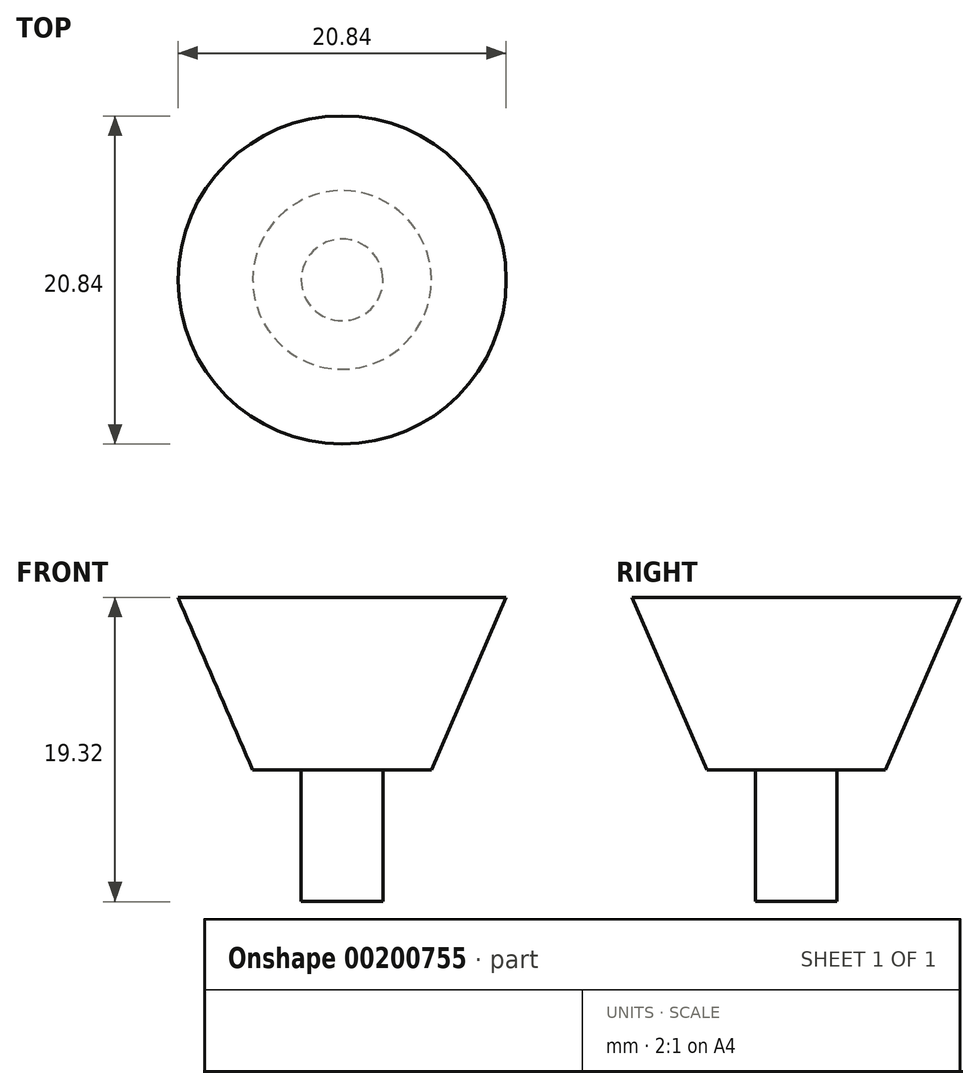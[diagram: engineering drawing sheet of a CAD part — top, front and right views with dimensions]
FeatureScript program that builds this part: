
annotation { "Feature Type Name" : "Feature", "Feature Type Description" : "" }
export const myFeature = defineFeature(function(context is Context, id is Id, definition is map)
    precondition{}
    {
        {
            var Q0;
            Q0=qCreatedBy(makeId("Front.planeOp"),FACE);
            var sketch = newSketch(context, id + "F0", { "sketchPlane" : qUnion([Q0])});
            skLineSegment(sketch, "E0", {"start": v(0, 0) * mm, "end": v(10.42, 0) * mm});
            skLineSegment(sketch, "E1", {"start": v(10.42, 0) * mm, "end": v(5.67, -10.95) * mm});
            skLineSegment(sketch, "E2", {"start": v(5.67, -10.95) * mm, "end": v(2.6, -10.95) * mm});
            skLineSegment(sketch, "E3", {"start": v(2.6, -10.95) * mm, "end": v(2.6, -19.32) * mm});
            skLineSegment(sketch, "E4", {"start": v(2.6, -19.32) * mm, "end": v(0, -19.32) * mm});
            skLineSegment(sketch, "E5", {"start": v(0, -19.32) * mm, "end": v(0, 0) * mm});
            skSolve(sketch);
        }
        {
            var Q0;
            Q0=makeQuery(id+"F0.imprint","IMPRINT",FACE,{"disambiguationData":[TD([[makeQuery(id+"F0.imprint","IMPRINT",EDGE,{"derivedFrom":sQuery(id+"F0.wireOp",EDGE,"E0")}),-1.0]])]});
            var Q1;
            Q1=sQuery(id+"F0.wireOp",EDGE,"E5");
            revolve(context, id + "F1", {"entities" : qUnion([Q0]), "axis" : qUnion([Q1]), "revolveType" : RevolveType.FULL});
        }
    });
